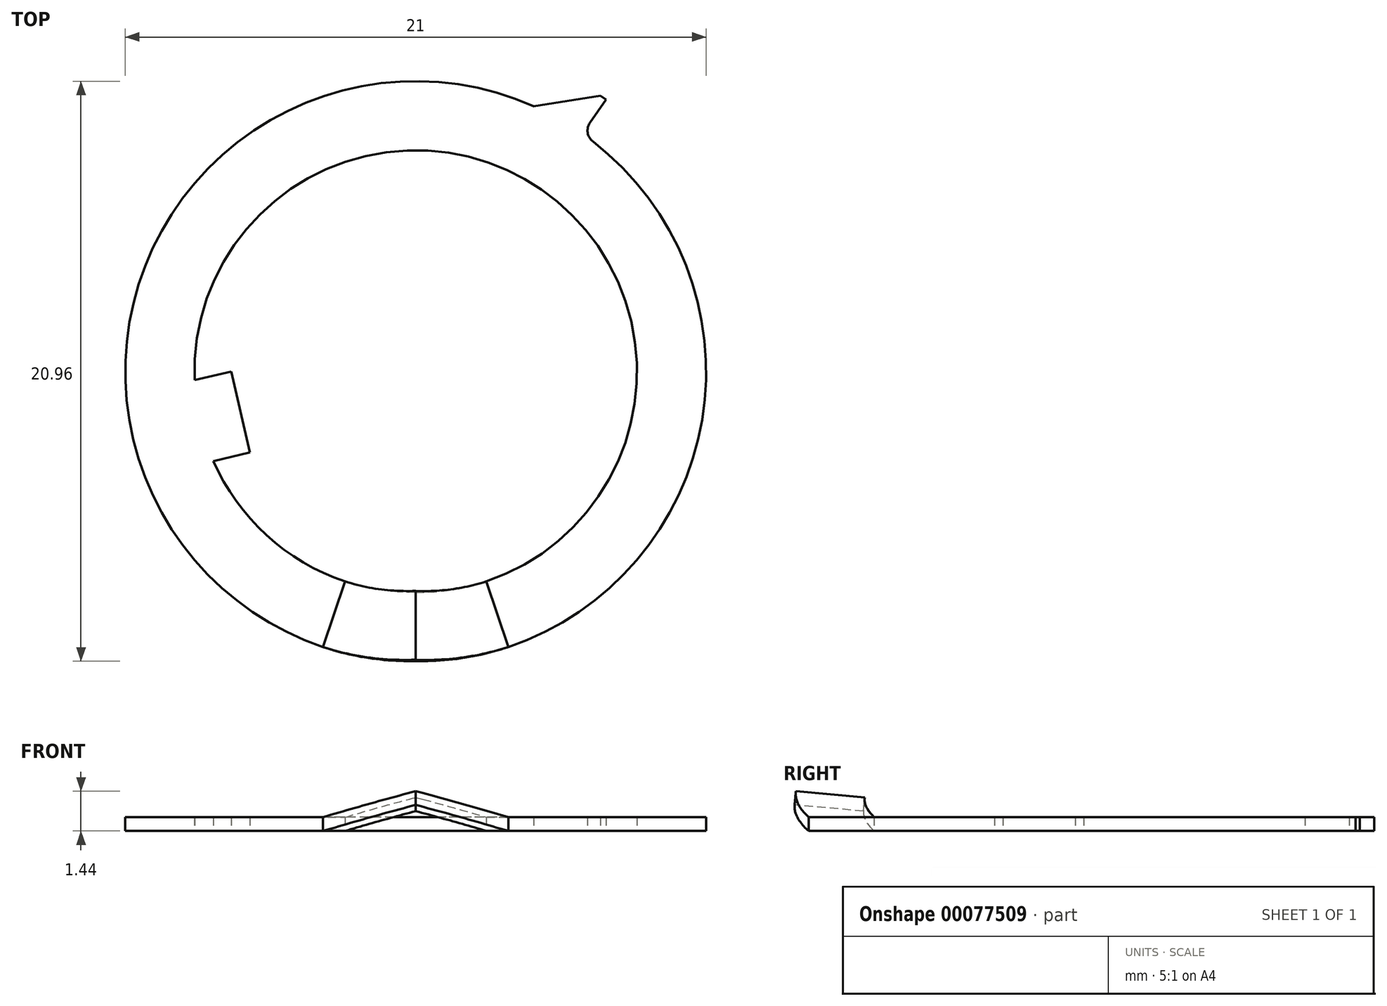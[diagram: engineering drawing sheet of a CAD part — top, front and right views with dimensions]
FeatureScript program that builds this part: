
annotation { "Feature Type Name" : "Feature", "Feature Type Description" : "" }
export const myFeature = defineFeature(function(context is Context, id is Id, definition is map)
    precondition{}
    {
        {
            var Q0;
            Q0=qCreatedBy(makeId("Top.planeOp"),FACE);
            var sketch = newSketch(context, id + "F0", { "sketchPlane" : qUnion([Q0])});
            skArc(sketch, "E0", {"start": v(4.27, 9.6) * mm, "mid": v(-9.78, 3.81) * mm, "end": v(-3.35, -9.95) * mm});
            skArc(sketch, "E1", {"start": v(-7.32, -3.23) * mm, "mid": v(-5.4, -5.9) * mm, "end": v(-2.55, -7.58) * mm});
            skLineSegment(sketch, "E2", {"start": v(0, 0) * mm, "end": v(-6.33, -1.46) * mm, "construction": true});
            skLineSegment(sketch, "E3", {"start": v(-6, -2.92) * mm, "end": v(-6.67, 0) * mm});
            skLineSegment(sketch, "E4", {"start": v(-6.67, 0) * mm, "end": v(-8, -0.3) * mm});
            skLineSegment(sketch, "E5", {"start": v(-6, -2.92) * mm, "end": v(-7.32, -3.23) * mm});
            skLineSegment(sketch, "E6", {"start": v(6.3, 9) * mm, "end": v(6.88, 9.83) * mm});
            skLineSegment(sketch, "E7", {"start": v(6.88, 9.83) * mm, "end": v(6.68, 9.97) * mm});
            skLineSegment(sketch, "E8", {"start": v(6.68, 9.97) * mm, "end": v(4.27, 9.6) * mm});
            skLineSegment(sketch, "E9", {"start": v(4.27, 9.6) * mm, "end": v(0, 0) * mm, "construction": true});
            skArc(sketch, "E10", {"start": v(6.3, 9) * mm, "mid": v(6.22, 8.64) * mm, "end": v(6.4, 8.32) * mm});
            skLineSegment(sketch, "E11", {"start": v(-2.55, -7.58) * mm, "end": v(-3.35, -9.95) * mm});
            skLineSegment(sketch, "E12", {"start": v(2.55, -7.58) * mm, "end": v(3.35, -9.95) * mm});
            skArc(sketch, "E13.trimOffspring", {"start": v(2.55, -7.58) * mm, "mid": v(4.54, 6.59) * mm, "end": v(-8, -0.3) * mm});
            skArc(sketch, "E14.trimOffspring", {"start": v(3.35, -9.95) * mm, "mid": v(10.36, -1.73) * mm, "end": v(6.4, 8.32) * mm});
            skLineSegment(sketch, "E15", {"start": v(0, 0) * mm, "end": v(0, 8) * mm, "construction": true});
            skSolve(sketch);
        }
        {
            var Q0;
            Q0=makeQuery(id+"F0.imprint","IMPRINT",FACE,{"disambiguationData":[TD([[makeQuery(id+"F0.imprint","IMPRINT",EDGE,{"derivedFrom":sQuery(id+"F0.wireOp",EDGE,"E0")}),1.0]])]});
            extrude(context, id + "F1", {"entities" : qUnion([Q0]), "depth" : 0.5 * mm});
        }
        {
            var Q0;
            Q0=sQuery(id+"F0.wireOp",EDGE,"E12");
            cPlane(context, id + "F2", {"entities" : qUnion([Q0]), "cplaneType" : CPlaneType.LINE_ANGLE, "offset" : 150 * mm, "angle" : 164.23 * degree, "width" : 150 * mm, "height" : 150 * mm});
        }
        {
            var Q0;
            Q0=qCreatedBy(id+"F2.planeOp",FACE);
            var sketch = newSketch(context, id + "F3", { "sketchPlane" : qUnion([Q0])});
            skArc(sketch, "E16", {"start": v(0, -8) * mm, "mid": v(1.34, -7.89) * mm, "end": v(2.64, -7.55) * mm});
            skArc(sketch, "E17", {"start": v(0, -10.5) * mm, "mid": v(1.76, -10.35) * mm, "end": v(3.47, -9.91) * mm});
            skLineSegment(sketch, "E18", {"start": v(0, 0) * mm, "end": v(0, -10.5) * mm});
            skLineSegment(sketch, "E19", {"start": v(2.64, -7.55) * mm, "end": v(3.47, -9.91) * mm});
            skSolve(sketch);
        }
        {
            var Q0;
            Q0=sQuery(id+"F0.wireOp",EDGE,"E11");
            cPlane(context, id + "F4", {"entities" : qUnion([Q0]), "cplaneType" : CPlaneType.LINE_ANGLE, "offset" : 150 * mm, "angle" : 15.77 * degree, "width" : 150 * mm, "height" : 150 * mm});
        }
        {
            var Q0;
            Q0=qCreatedBy(id+"F4.planeOp",FACE);
            var sketch = newSketch(context, id + "F5", { "sketchPlane" : qUnion([Q0])});
            skArc(sketch, "E20", {"start": v(0, 8) * mm, "mid": v(-1.34, 7.89) * mm, "end": v(-2.64, 7.55) * mm});
            skArc(sketch, "E21", {"start": v(0, 10.5) * mm, "mid": v(-1.76, 10.35) * mm, "end": v(-3.47, 9.91) * mm});
            skLineSegment(sketch, "E22", {"start": v(-3.47, 9.91) * mm, "end": v(-2.64, 7.55) * mm});
            skLineSegment(sketch, "E23", {"start": v(0, 8) * mm, "end": v(0, 10.5) * mm});
            skSolve(sketch);
        }
        {
            var Q0;
            Q0=makeQuery(id+"F1.opExtrude","SWEPT_FACE",FACE,{"disambiguationData":[OSD([sQuery(id+"F0.wireOp",EDGE,"E11")])]});
            var Q1;
            Q1=sQuery(id+"F5.wireOp",EDGE,"E21");
            var Q2;
            Q2=sQuery(id+"F3.wireOp",EDGE,"E17");
            sweep(context, id + "F6", {"operationType" : NewBodyOperationType.ADD, "profiles" : qUnion([Q0]), "path" : qUnion([Q1, Q2])});
        }
    });
